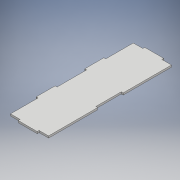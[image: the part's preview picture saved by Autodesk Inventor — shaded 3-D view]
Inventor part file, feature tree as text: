
AUTODESK INVENTOR PART (.ipt)
format: ipt  version: 2017 (Build 210142000, 142)  size: 139,264 bytes
history: native  units: mm
features: extrude x1, sketch x1
ambient origin geometry x8: Origin, YZ Plane, XZ Plane, XY Plane, X Axis, Y Axis, Z Axis, Center Point
bodies: Solid1 (feature_tree)
feature tree (2):
  extrude  "Extrusion1"  [1 undecoded]
  sketch  "Sketch1"  dims[d26=3.0mm d27=0.0mm d47=193.0mm d48=60.0mm d49=3.0mm d50=30.0mm d51=15.0mm d52=3.0mm d53=3.0mm d54=15.0mm d55=3.0mm d56=3.0mm d57=3.0mm d58=3.0mm d59=15.0mm d60=40.0mm d61=3.0mm d62=77.0mm d63=3.0mm d64=76.0mm d65=199.145723mm d66=43.3mm d67=46.6mm d68=43.3mm d69=30.0mm d70=29.8mm]
note: 1 required parameter value undecoded (feature->parameter linkage not recoverable at this tier; creation-order binding heuristic only, values carry confidence <= 0.55)
